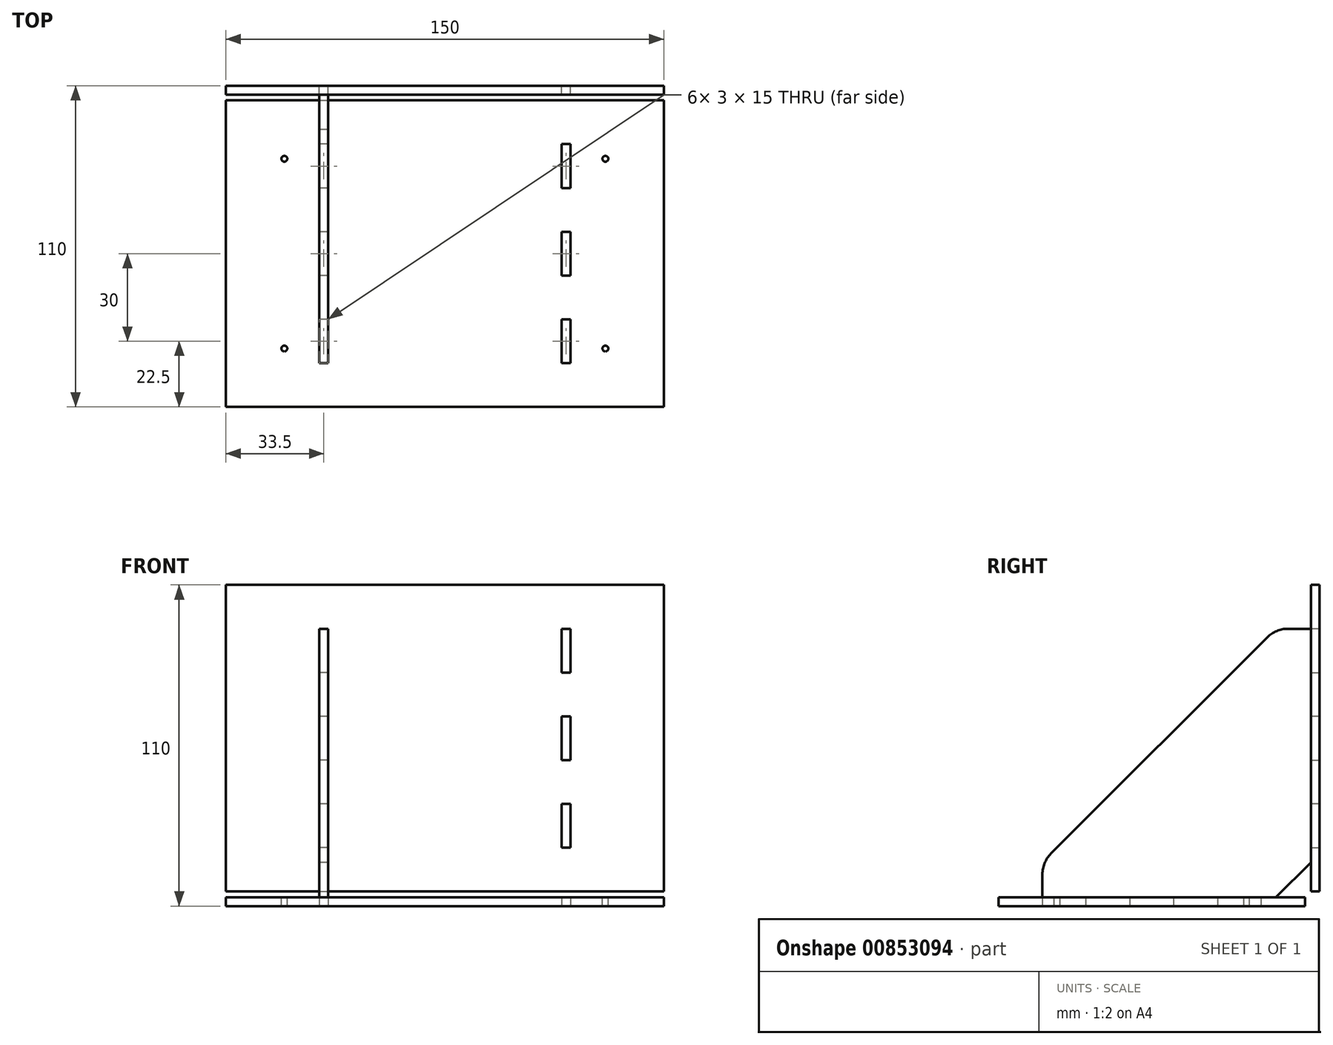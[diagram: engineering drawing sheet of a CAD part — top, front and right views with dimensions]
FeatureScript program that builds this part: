
annotation { "Feature Type Name" : "Feature", "Feature Type Description" : "" }
export const myFeature = defineFeature(function(context is Context, id is Id, definition is map)
    precondition{}
    {
        {
            var Q0;
            Q0=qCreatedBy(makeId("Top.planeOp"),FACE);
            var sketch = newSketch(context, id + "F0", { "sketchPlane" : qUnion([Q0])});
            skLineSegment(sketch, "E0.bottom", {"start": v(-75, -5) * mm, "end": v(75, -5) * mm});
            skLineSegment(sketch, "E0.top", {"start": v(-75, -110) * mm, "end": v(75, -110) * mm});
            skLineSegment(sketch, "E0.left", {"start": v(-75, -5) * mm, "end": v(-75, -110) * mm});
            skLineSegment(sketch, "E0.right", {"start": v(75, -5) * mm, "end": v(75, -110) * mm});
            skLineSegment(sketch, "E1.bottom", {"start": v(-43, -20) * mm, "end": v(-40, -20) * mm});
            skLineSegment(sketch, "E1.top", {"start": v(-43, -35) * mm, "end": v(-40, -35) * mm});
            skLineSegment(sketch, "E1.left", {"start": v(-43, -20) * mm, "end": v(-43, -35) * mm});
            skLineSegment(sketch, "E1.right", {"start": v(-40, -20) * mm, "end": v(-40, -35) * mm});
            skLineSegment(sketch, "E2.bottom", {"start": v(-43, -50) * mm, "end": v(-40, -50) * mm});
            skLineSegment(sketch, "E2.top", {"start": v(-43, -65) * mm, "end": v(-40, -65) * mm});
            skLineSegment(sketch, "E2.left", {"start": v(-43, -50) * mm, "end": v(-43, -65) * mm});
            skLineSegment(sketch, "E2.right", {"start": v(-40, -50) * mm, "end": v(-40, -65) * mm});
            skLineSegment(sketch, "E3.bottom", {"start": v(-43, -80) * mm, "end": v(-40, -80) * mm});
            skLineSegment(sketch, "E3.top", {"start": v(-43, -95) * mm, "end": v(-40, -95) * mm});
            skLineSegment(sketch, "E3.left", {"start": v(-43, -80) * mm, "end": v(-43, -95) * mm});
            skLineSegment(sketch, "E3.right", {"start": v(-40, -80) * mm, "end": v(-40, -95) * mm});
            skLineSegment(sketch, "E4.MirrorCS", {"start": v(43, -20) * mm, "end": v(40, -20) * mm});
            skLineSegment(sketch, "E5.MirrorCS", {"start": v(43, -95) * mm, "end": v(40, -95) * mm});
            skLineSegment(sketch, "E6.MirrorCS", {"start": v(43, -50) * mm, "end": v(40, -50) * mm});
            skLineSegment(sketch, "E7.MirrorCS", {"start": v(43, -35) * mm, "end": v(40, -35) * mm});
            skLineSegment(sketch, "E8.MirrorCS", {"start": v(43, -65) * mm, "end": v(40, -65) * mm});
            skLineSegment(sketch, "E9.MirrorCS", {"start": v(43, -80) * mm, "end": v(40, -80) * mm});
            skLineSegment(sketch, "E10.MirrorCS", {"start": v(40, -80) * mm, "end": v(40, -95) * mm});
            skLineSegment(sketch, "E11.MirrorCS", {"start": v(40, -20) * mm, "end": v(40, -35) * mm});
            skLineSegment(sketch, "E12.MirrorCS", {"start": v(40, -50) * mm, "end": v(40, -65) * mm});
            skLineSegment(sketch, "E13.MirrorCS", {"start": v(43, -80) * mm, "end": v(43, -95) * mm});
            skLineSegment(sketch, "E14.MirrorCS", {"start": v(43, -20) * mm, "end": v(43, -35) * mm});
            skLineSegment(sketch, "E15.MirrorCS", {"start": v(43, -50) * mm, "end": v(43, -65) * mm});
            skSolve(sketch);
        }
        {
            var Q0;
            Q0 = qSketchRegion(id + "F0", true);
            extrude(context, id + "F1", {"entities" : qUnion([Q0]), "depth" : 3 * mm, "offsetDistance" : 25 * mm});
        }
        {
            var Q0;
            Q0=qCreatedBy(makeId("Top.planeOp"),FACE);
            var sketch = newSketch(context, id + "F2", { "sketchPlane" : qUnion([Q0])});
            skLineSegment(sketch, "E16", {"start": v(0, 0) * mm, "end": v(31.18, 0) * mm});
            skSolve(sketch);
        }
        {
            var Q0;
            Q0=qCreatedBy(makeId("Front.planeOp"),FACE);
            var Q1;
            Q1=sQuery(id+"F2.wireOp",EDGE,"E16");
            cPlane(context, id + "F3", {"entities" : qUnion([Q0, Q1]), "cplaneType" : CPlaneType.LINE_ANGLE, "offset" : 25 * mm, "angle" : 45 * degree, "width" : 150 * mm, "height" : 150 * mm});
        }
        {
            var Q0;
            Q0=makeQuery(id+"F1.opExtrude","SWEPT_BODY",BODY,{"disambiguationData":[OSD([sQuery(id+"F0.wireOp",EDGE,"E0.bottom"),sQuery(id+"F0.wireOp",EDGE,"E0.top"),sQuery(id+"F0.wireOp",EDGE,"E0.left"),sQuery(id+"F0.wireOp",EDGE,"E0.right"),sQuery(id+"F0.wireOp",EDGE,"E1.bottom"),sQuery(id+"F0.wireOp",EDGE,"E1.top"),sQuery(id+"F0.wireOp",EDGE,"E1.left"),sQuery(id+"F0.wireOp",EDGE,"E1.right"),sQuery(id+"F0.wireOp",EDGE,"E2.bottom"),sQuery(id+"F0.wireOp",EDGE,"E2.top"),sQuery(id+"F0.wireOp",EDGE,"E2.left"),sQuery(id+"F0.wireOp",EDGE,"E2.right"),sQuery(id+"F0.wireOp",EDGE,"E3.bottom"),sQuery(id+"F0.wireOp",EDGE,"E3.top"),sQuery(id+"F0.wireOp",EDGE,"E3.left"),sQuery(id+"F0.wireOp",EDGE,"E3.right"),sQuery(id+"F0.wireOp",EDGE,"E4.MirrorCS"),sQuery(id+"F0.wireOp",EDGE,"E5.MirrorCS"),sQuery(id+"F0.wireOp",EDGE,"E6.MirrorCS"),sQuery(id+"F0.wireOp",EDGE,"E7.MirrorCS"),sQuery(id+"F0.wireOp",EDGE,"E8.MirrorCS"),sQuery(id+"F0.wireOp",EDGE,"E9.MirrorCS"),sQuery(id+"F0.wireOp",EDGE,"E10.MirrorCS"),sQuery(id+"F0.wireOp",EDGE,"E11.MirrorCS"),sQuery(id+"F0.wireOp",EDGE,"E12.MirrorCS"),sQuery(id+"F0.wireOp",EDGE,"E13.MirrorCS"),sQuery(id+"F0.wireOp",EDGE,"E14.MirrorCS"),sQuery(id+"F0.wireOp",EDGE,"E15.MirrorCS")])]});
            var Q1;
            Q1=qCreatedBy(id+"F3.planeOp",FACE);
            mirror(context, id + "F4", {"entities" : qUnion([Q0]), "mirrorPlane" : qUnion([Q1])});
        }
        {
            var Q0;
            Q0=makeQuery(id+"F4.opPattern","COPY",FACE,{"derivedFrom":makeQuery(id+"F1.opExtrude","SWEPT_FACE",FACE,{"disambiguationData":[OSD([sQuery(id+"F0.wireOp",EDGE,"E3.left")])]}),"instanceName":"1"});
            var sketch = newSketch(context, id + "F5", { "sketchPlane" : qUnion([Q0])});
            skLineSegment(sketch, "E17", {"start": v(0, 95) * mm, "end": v(-15, 95) * mm});
            skLineSegment(sketch, "E18", {"start": v(-15, 95) * mm, "end": v(-95, 15) * mm});
            skLineSegment(sketch, "E19", {"start": v(-95, 15) * mm, "end": v(-95, 0) * mm});
            skLineSegment(sketch, "E20", {"start": v(-95, 0) * mm, "end": v(-80, 0) * mm});
            skLineSegment(sketch, "E21", {"start": v(-80, 0) * mm, "end": v(-80, 3) * mm});
            skLineSegment(sketch, "E22", {"start": v(-80, 3) * mm, "end": v(-65, 3) * mm});
            skLineSegment(sketch, "E23", {"start": v(-65, 3) * mm, "end": v(-65, 0) * mm});
            skLineSegment(sketch, "E24", {"start": v(-65, 0) * mm, "end": v(-50, 0) * mm});
            skLineSegment(sketch, "E25", {"start": v(-50, 0) * mm, "end": v(-50, 3) * mm});
            skLineSegment(sketch, "E26", {"start": v(-50, 3) * mm, "end": v(-35, 3) * mm});
            skLineSegment(sketch, "E27", {"start": v(-35, 3) * mm, "end": v(-35, 0) * mm});
            skLineSegment(sketch, "E28", {"start": v(-35, 0) * mm, "end": v(-20, 0) * mm});
            skLineSegment(sketch, "E29", {"start": v(-20, 0) * mm, "end": v(-20, 3) * mm});
            skLineSegment(sketch, "E30", {"start": v(-20, 3) * mm, "end": v(-15, 3) * mm});
            skLineSegment(sketch, "E31", {"start": v(-15, 3) * mm, "end": v(-3, 15) * mm});
            skLineSegment(sketch, "E32", {"start": v(-3, 15) * mm, "end": v(-3, 20) * mm});
            skLineSegment(sketch, "E33", {"start": v(-3, 20) * mm, "end": v(0, 20) * mm});
            skLineSegment(sketch, "E34", {"start": v(0, 20) * mm, "end": v(0, 35) * mm});
            skLineSegment(sketch, "E35", {"start": v(0, 35) * mm, "end": v(-3, 35) * mm});
            skLineSegment(sketch, "E36", {"start": v(-3, 35) * mm, "end": v(-3, 50) * mm});
            skLineSegment(sketch, "E37", {"start": v(-3, 50) * mm, "end": v(0, 50) * mm});
            skLineSegment(sketch, "E38", {"start": v(0, 50) * mm, "end": v(0, 65) * mm});
            skLineSegment(sketch, "E39", {"start": v(0, 65) * mm, "end": v(-3, 65) * mm});
            skLineSegment(sketch, "E40", {"start": v(-3, 65) * mm, "end": v(-3, 80) * mm});
            skLineSegment(sketch, "E41", {"start": v(-3, 80) * mm, "end": v(0, 80) * mm});
            skLineSegment(sketch, "E42", {"start": v(0, 80) * mm, "end": v(0, 95) * mm});
            skSolve(sketch);
        }
        {
            var Q0;
            Q0 = qSketchRegion(id + "F5", true);
            extrude(context, id + "F6", {"entities" : qUnion([Q0]), "depth" : 3 * mm, "offsetDistance" : 25 * mm});
        }
        {
            var Q0;
            Q0=makeQuery(id+"F6.opExtrude","SWEPT_EDGE",EDGE,{"disambiguationData":[OSD([sQuery(id+"F5.wireOp",EDGE,"E17"),sQuery(id+"F5.wireOp",EDGE,"E18")])]});
            var Q1;
            Q1=makeQuery(id+"F6.opExtrude","SWEPT_EDGE",EDGE,{"disambiguationData":[OSD([sQuery(id+"F5.wireOp",EDGE,"E18"),sQuery(id+"F5.wireOp",EDGE,"E19")])]});
            fillet(context, id + "F7", {"entities" : qUnion([Q0, Q1]), "radius" : 10 * mm, "tangentPropagation" : true, "allowEdgeOverflow" : false});
        }
        {
            var Q0;
            Q0=makeQuery(id+"F1.opExtrude","CAP_FACE",FACE,{"disambiguationData":[OSD([sQuery(id+"F0.wireOp",EDGE,"E0.bottom"),sQuery(id+"F0.wireOp",EDGE,"E0.top"),sQuery(id+"F0.wireOp",EDGE,"E0.left"),sQuery(id+"F0.wireOp",EDGE,"E0.right"),sQuery(id+"F0.wireOp",EDGE,"E1.bottom"),sQuery(id+"F0.wireOp",EDGE,"E1.top"),sQuery(id+"F0.wireOp",EDGE,"E1.left"),sQuery(id+"F0.wireOp",EDGE,"E1.right"),sQuery(id+"F0.wireOp",EDGE,"E2.bottom"),sQuery(id+"F0.wireOp",EDGE,"E2.top"),sQuery(id+"F0.wireOp",EDGE,"E2.left"),sQuery(id+"F0.wireOp",EDGE,"E2.right"),sQuery(id+"F0.wireOp",EDGE,"E3.bottom"),sQuery(id+"F0.wireOp",EDGE,"E3.top"),sQuery(id+"F0.wireOp",EDGE,"E3.left"),sQuery(id+"F0.wireOp",EDGE,"E3.right"),sQuery(id+"F0.wireOp",EDGE,"E4.MirrorCS"),sQuery(id+"F0.wireOp",EDGE,"E5.MirrorCS"),sQuery(id+"F0.wireOp",EDGE,"E6.MirrorCS"),sQuery(id+"F0.wireOp",EDGE,"E7.MirrorCS"),sQuery(id+"F0.wireOp",EDGE,"E8.MirrorCS"),sQuery(id+"F0.wireOp",EDGE,"E9.MirrorCS"),sQuery(id+"F0.wireOp",EDGE,"E10.MirrorCS"),sQuery(id+"F0.wireOp",EDGE,"E11.MirrorCS"),sQuery(id+"F0.wireOp",EDGE,"E12.MirrorCS"),sQuery(id+"F0.wireOp",EDGE,"E13.MirrorCS"),sQuery(id+"F0.wireOp",EDGE,"E14.MirrorCS"),sQuery(id+"F0.wireOp",EDGE,"E15.MirrorCS")])],"isStart":false});
            var sketch = newSketch(context, id + "F8", { "sketchPlane" : qUnion([Q0])});
            skCircle(sketch, "E43", {"center": v(-55, -25) * mm, "radius": 1 * mm});
            skCircle(sketch, "E44", {"center": v(-55, -90) * mm, "radius": 1 * mm});
            skCircle(sketch, "E45.MirrorC", {"center": v(55, -25) * mm, "radius": 1 * mm});
            skCircle(sketch, "E46.MirrorC", {"center": v(55, -90) * mm, "radius": 1 * mm});
            skSolve(sketch);
        }
        {
            var Q0;
            Q0 = qSketchRegion(id + "F8", true);
            extrude(context, id + "F9", {"entities" : qUnion([Q0]), "operationType" : NewBodyOperationType.REMOVE, "oppositeDirection" : true, "depth" : 25 * mm, "offsetDistance" : 25 * mm});
        }
    });
